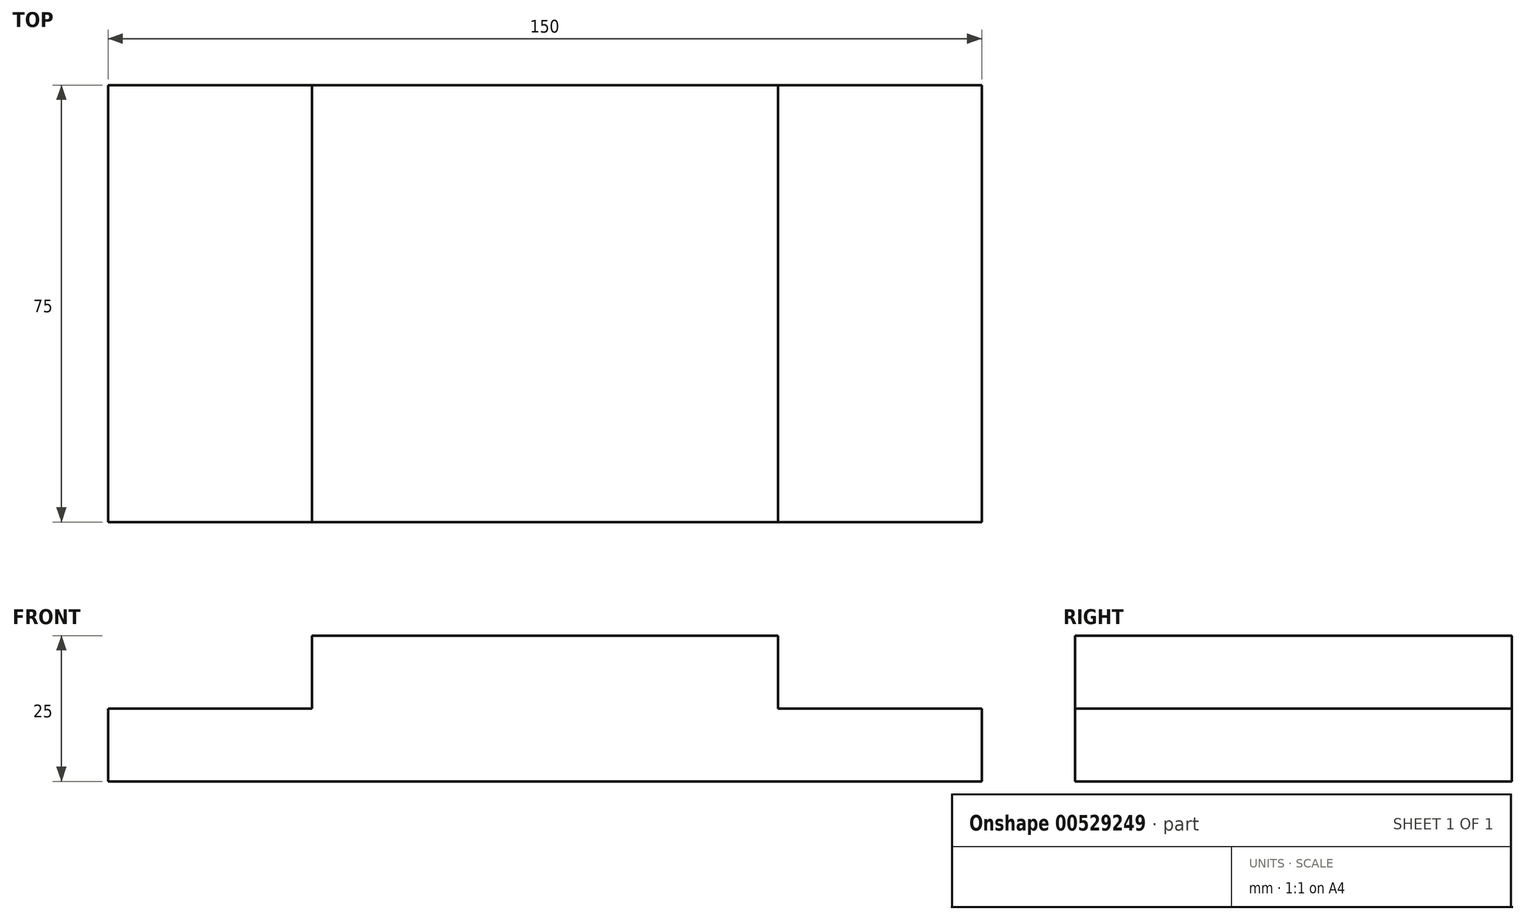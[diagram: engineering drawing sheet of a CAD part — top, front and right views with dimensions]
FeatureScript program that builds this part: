
annotation { "Feature Type Name" : "Feature", "Feature Type Description" : "" }
export const myFeature = defineFeature(function(context is Context, id is Id, definition is map)
    precondition{}
    {
        {
            var Q0;
            Q0=qCreatedBy(makeId("Top.planeOp"),FACE);
            var sketch = newSketch(context, id + "F0", { "sketchPlane" : qUnion([Q0])});
            skLineSegment(sketch, "E0.bottom", {"start": v(75, -37.5) * mm, "end": v(-75, -37.5) * mm});
            skLineSegment(sketch, "E0.top", {"start": v(75, 37.5) * mm, "end": v(-75, 37.5) * mm});
            skLineSegment(sketch, "E0.left", {"start": v(75, -37.5) * mm, "end": v(75, 37.5) * mm});
            skLineSegment(sketch, "E0.right", {"start": v(-75, -37.5) * mm, "end": v(-75, 37.5) * mm});
            skPoint(sketch, "E0.middle", {"position": v(0, 0) * mm});
            skSolve(sketch);
        }
        {
            var Q0;
            Q0 = qSketchRegion(id + "F0", true);
            extrude(context, id + "F1", {"entities" : qUnion([Q0]), "depth" : 25 * mm, "offsetDistance" : 25 * mm});
        }
        {
            var Q0;
            Q0=makeQuery(id+"F1.opExtrude","CAP_FACE",FACE,{"disambiguationData":[OSD([sQuery(id+"F0.wireOp",EDGE,"E0.bottom"),sQuery(id+"F0.wireOp",EDGE,"E0.top"),sQuery(id+"F0.wireOp",EDGE,"E0.left"),sQuery(id+"F0.wireOp",EDGE,"E0.right")])],"isStart":false});
            var sketch = newSketch(context, id + "F2", { "sketchPlane" : qUnion([Q0])});
            skLineSegment(sketch, "E1.bottom", {"start": v(-75, 37.5) * mm, "end": v(-40, 37.5) * mm});
            skLineSegment(sketch, "E1.top", {"start": v(-75, -37.5) * mm, "end": v(-40, -37.5) * mm});
            skLineSegment(sketch, "E1.left", {"start": v(-75, 37.5) * mm, "end": v(-75, -37.5) * mm});
            skLineSegment(sketch, "E1.right", {"start": v(-40, 37.5) * mm, "end": v(-40, -37.5) * mm});
            skLineSegment(sketch, "E2.bottom", {"start": v(75, -37.5) * mm, "end": v(40, -37.5) * mm});
            skLineSegment(sketch, "E2.top", {"start": v(75, 37.5) * mm, "end": v(40, 37.5) * mm});
            skLineSegment(sketch, "E2.left", {"start": v(75, -37.5) * mm, "end": v(75, 37.5) * mm});
            skLineSegment(sketch, "E2.right", {"start": v(40, -37.5) * mm, "end": v(40, 37.5) * mm});
            skSolve(sketch);
        }
        {
            var Q0;
            Q0 = qSketchRegion(id + "F2", true);
            extrude(context, id + "F3", {"entities" : qUnion([Q0]), "operationType" : NewBodyOperationType.REMOVE, "oppositeDirection" : true, "depth" : 12.5 * mm, "offsetDistance" : 25 * mm});
        }
    });
